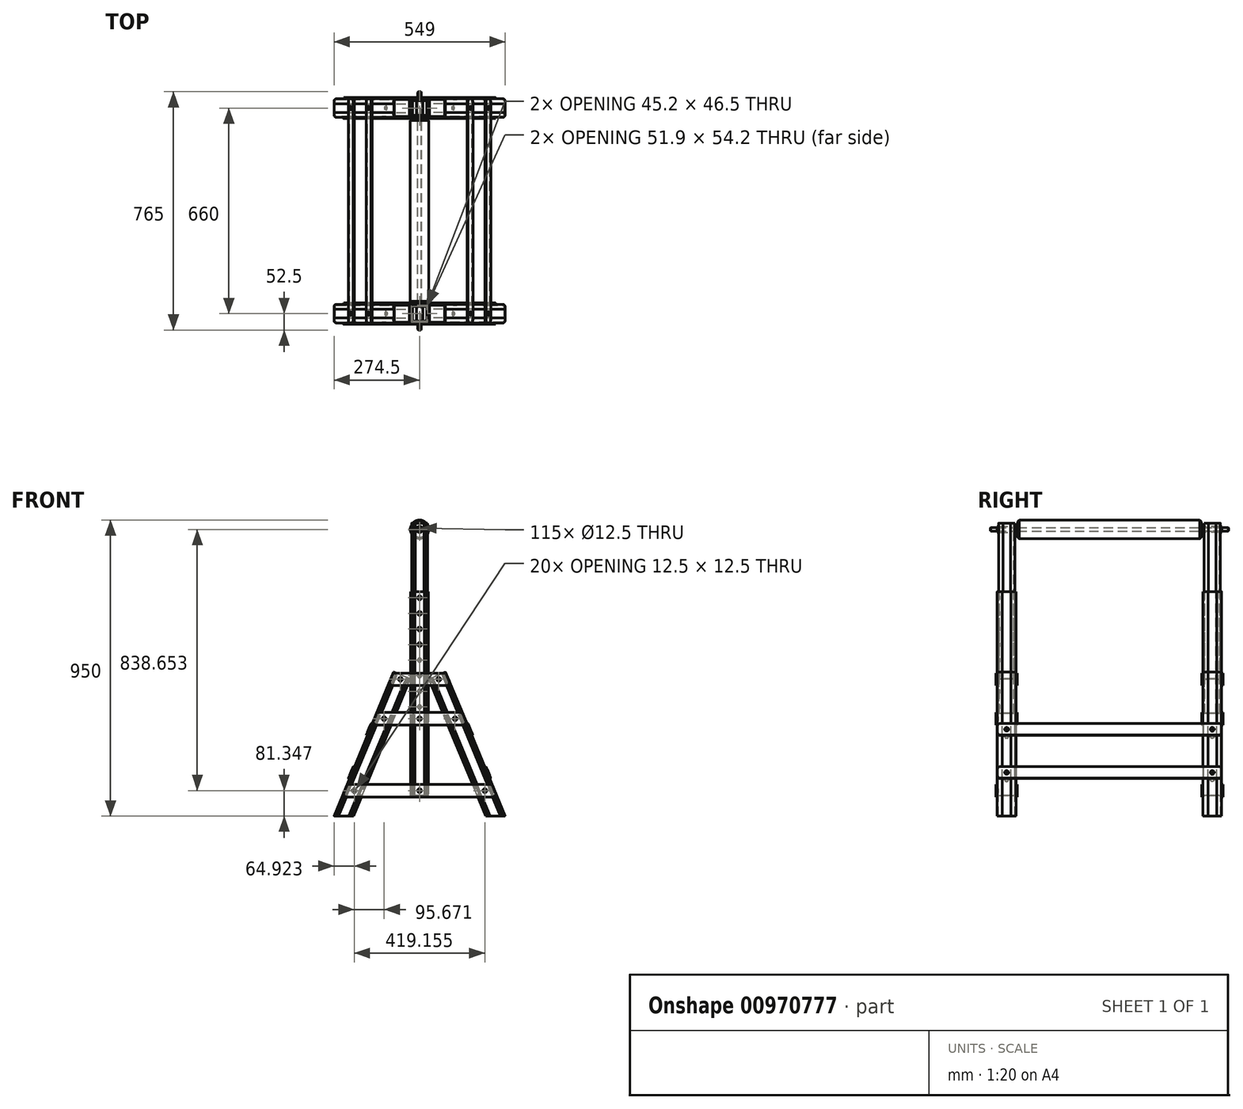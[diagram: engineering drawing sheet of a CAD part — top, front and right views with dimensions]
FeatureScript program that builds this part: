
annotation { "Feature Type Name" : "Feature", "Feature Type Description" : "" }
export const myFeature = defineFeature(function(context is Context, id is Id, definition is map)
    precondition{}
    {
        {
            var Q0;
            Q0=qCreatedBy(makeId("Front.planeOp"),FACE);
            var sketch = newSketch(context, id + "F0", { "sketchPlane" : qUnion([Q0])});
            skLineSegment(sketch, "E0", {"start": v(0, 0) * mm, "end": v(-62.45, 0) * mm});
            skLineSegment(sketch, "E1", {"start": v(-62.45, 0) * mm, "end": v(-244.65, 439.86) * mm});
            skLineSegment(sketch, "E2", {"start": v(-244.65, 439.86) * mm, "end": v(-191.34, 461.94) * mm});
            skLineSegment(sketch, "E3", {"start": v(-191.34, 461.94) * mm, "end": v(0, 0) * mm});
            skLineSegment(sketch, "E4", {"start": v(-218, 450.9) * mm, "end": v(-31.23, 0) * mm, "construction": true});
            skCircle(sketch, "E5", {"center": v(-213.02, 438.89) * mm, "radius": 6.25 * mm});
            skCircle(sketch, "E6", {"center": v(-64.92, 81.35) * mm, "radius": 6.25 * mm});
            skCircle(sketch, "E7", {"center": v(-160.6, 312.32) * mm, "radius": 6.25 * mm});
            skSolve(sketch);
        }
        {
            var Q0;
            Q0=qSketchRegion(id+"F0",true);
            extrude(context, id + "F1", {"entities" : qUnion([Q0]), "depth" : 60 * mm, "offsetDistance" : 25 * mm});
        }
        {
            var Q0;
            Q0=makeQuery(id+"F1.opExtrude","SWEPT_FACE",FACE,{"disambiguationData":[OSD([sQuery(id+"F0.wireOp",EDGE,"E3")])]});
            var sketch = newSketch(context, id + "F2", { "sketchPlane" : qUnion([Q0])});
            skLineSegment(sketch, "E8", {"start": v(-30, 500) * mm, "end": v(-30, 0) * mm, "construction": true});
            skCircle(sketch, "E9", {"center": v(-30, 150) * mm, "radius": 6.25 * mm});
            skCircle(sketch, "E10", {"center": v(-30, 300) * mm, "radius": 6.25 * mm});
            skSolve(sketch);
        }
        {
            var Q0;
            Q0=qSketchRegion(id+"F2",true);
            var Q1;
            Q1=makeQuery(id+"F1.opExtrude","SWEPT_FACE",FACE,{"disambiguationData":[OSD([sQuery(id+"F0.wireOp",EDGE,"E1")])]});
            extrude(context, id + "F3", {"entities" : qUnion([Q0]), "operationType" : NewBodyOperationType.REMOVE, "endBound" : BoundingType.UP_TO_SURFACE, "oppositeDirection" : true, "depth" : 25 * mm, "endBoundEntityFace" : qUnion([Q1]), "offsetDistance" : 25 * mm});
        }
        {
            var Q0;
            Q0=makeQuery(id+"F1.opExtrude","CAP_EDGE",EDGE,{"disambiguationData":[OSD([sQuery(id+"F0.wireOp",EDGE,"E1")])],"isStart":false});
            var Q1;
            Q1=makeQuery(id+"F1.opExtrude","CAP_EDGE",EDGE,{"disambiguationData":[OSD([sQuery(id+"F0.wireOp",EDGE,"E3")])],"isStart":false});
            var Q2;
            Q2=makeQuery(id+"F1.opExtrude","CAP_EDGE",EDGE,{"disambiguationData":[OSD([sQuery(id+"F0.wireOp",EDGE,"E1")])],"isStart":true});
            var Q3;
            Q3=makeQuery(id+"F1.opExtrude","CAP_EDGE",EDGE,{"disambiguationData":[OSD([sQuery(id+"F0.wireOp",EDGE,"E3")])],"isStart":true});
            fillet(context, id + "F4", {"entities" : qUnion([Q0, Q1, Q2, Q3]), "radius" : 7.5 * mm, "tangentPropagation" : true, "allowEdgeOverflow" : false});
        }
        {
            var Q0;
            Q0=makeQuery(id+"F1.opExtrude","SWEPT_FACE",FACE,{"disambiguationData":[OSD([sQuery(id+"F0.wireOp",EDGE,"E2")])]});
            var sketch = newSketch(context, id + "F5", { "sketchPlane" : qUnion([Q0])});
            skLineSegment(sketch, "E11", {"start": v(-57.7, -30) * mm, "end": v(-28.85, -30) * mm, "construction": true});
            skLineSegment(sketch, "E12", {"start": v(-28.85, -30) * mm, "end": v(-28.85, -60) * mm, "construction": true});
            skArc(sketch, "E13.0", {"start": v(-54.8, -52.5) * mm, "mid": v(-53.45, -55.75) * mm, "end": v(-50.2, -57.1) * mm});
            skLineSegment(sketch, "E14", {"start": v(-57.4, -30) * mm, "end": v(-57.4, -44) * mm});
            skLineSegment(sketch, "E15", {"start": v(-57.4, -44) * mm, "end": v(-57.7, -44) * mm});
            skLineSegment(sketch, "E16", {"start": v(-50.2, -60) * mm, "end": v(-49.2, -59) * mm});
            skLineSegment(sketch, "E17", {"start": v(-49.2, -59) * mm, "end": v(-48.2, -60) * mm});
            skLineSegment(sketch, "E18", {"start": v(-48.2, -60) * mm, "end": v(-47.2, -59) * mm});
            skLineSegment(sketch, "E19", {"start": v(-47.2, -59) * mm, "end": v(-46.2, -60) * mm});
            skLineSegment(sketch, "E20", {"start": v(-46.2, -60) * mm, "end": v(-45.2, -59) * mm});
            skLineSegment(sketch, "E21", {"start": v(-45.2, -59) * mm, "end": v(-44.2, -60) * mm});
            skLineSegment(sketch, "E22", {"start": v(-50.2, -57.1) * mm, "end": v(-28.85, -57.1) * mm});
            skLineSegment(sketch, "E23", {"start": v(-54.8, -52.5) * mm, "end": v(-54.8, -30) * mm});
            skLineSegment(sketch, "E24.MirrorCS", {"start": v(-0.3, -44) * mm, "end": v(0, -44) * mm});
            skLineSegment(sketch, "E25.MirrorCS", {"start": v(-12.5, -59) * mm, "end": v(-13.5, -60) * mm});
            skLineSegment(sketch, "E26.MirrorCS", {"start": v(-7.5, -60) * mm, "end": v(-8.5, -59) * mm});
            skLineSegment(sketch, "E27.MirrorCS", {"start": v(-8.5, -59) * mm, "end": v(-9.5, -60) * mm});
            skLineSegment(sketch, "E28.MirrorCS", {"start": v(-11.5, -60) * mm, "end": v(-12.5, -59) * mm});
            skLineSegment(sketch, "E29.MirrorCS", {"start": v(-10.5, -59) * mm, "end": v(-11.5, -60) * mm});
            skLineSegment(sketch, "E30.MirrorCS", {"start": v(-9.5, -60) * mm, "end": v(-10.5, -59) * mm});
            skLineSegment(sketch, "E31.MirrorCS", {"start": v(-0.3, -30) * mm, "end": v(-0.3, -44) * mm});
            skLineSegment(sketch, "E32.MirrorCS", {"start": v(-7.5, -57.1) * mm, "end": v(-28.85, -57.1) * mm});
            skLineSegment(sketch, "E33.MirrorCS", {"start": v(-2.9, -52.5) * mm, "end": v(-2.9, -30) * mm});
            skArc(sketch, "E34.MirrorCS", {"start": v(-2.9, -52.5) * mm, "mid": v(-4.25, -55.75) * mm, "end": v(-7.5, -57.1) * mm});
            skLineSegment(sketch, "E35.MirrorCS", {"start": v(-57.4, -16) * mm, "end": v(-57.7, -16) * mm});
            skLineSegment(sketch, "E36.MirrorCS", {"start": v(-50.2, 0) * mm, "end": v(-49.2, -1) * mm});
            skLineSegment(sketch, "E37.MirrorCS", {"start": v(-45.2, -1) * mm, "end": v(-44.2, 0) * mm});
            skLineSegment(sketch, "E38.MirrorCS", {"start": v(-47.2, -1) * mm, "end": v(-46.2, 0) * mm});
            skLineSegment(sketch, "E39.MirrorCS", {"start": v(-48.2, 0) * mm, "end": v(-47.2, -1) * mm});
            skLineSegment(sketch, "E40.MirrorCS", {"start": v(-49.2, -1) * mm, "end": v(-48.2, 0) * mm});
            skLineSegment(sketch, "E41.MirrorCS", {"start": v(-46.2, 0) * mm, "end": v(-45.2, -1) * mm});
            skLineSegment(sketch, "E42.MirrorCS", {"start": v(-57.4, -30) * mm, "end": v(-57.4, -16) * mm});
            skArc(sketch, "E43.MirrorCS", {"start": v(-54.8, -7.5) * mm, "mid": v(-53.45, -4.25) * mm, "end": v(-50.2, -2.9) * mm});
            skLineSegment(sketch, "E44.MirrorCS", {"start": v(-50.2, -2.9) * mm, "end": v(-28.85, -2.9) * mm});
            skLineSegment(sketch, "E45.MirrorCS", {"start": v(-54.8, -7.5) * mm, "end": v(-54.8, -30) * mm});
            skLineSegment(sketch, "E46.MirrorCS", {"start": v(-0.3, -16) * mm, "end": v(0, -16) * mm});
            skLineSegment(sketch, "E47.MirrorCS", {"start": v(-8.5, -1) * mm, "end": v(-9.5, 0) * mm});
            skLineSegment(sketch, "E48.MirrorCS", {"start": v(-11.5, 0) * mm, "end": v(-12.5, -1) * mm});
            skLineSegment(sketch, "E49.MirrorCS", {"start": v(-10.5, -1) * mm, "end": v(-11.5, 0) * mm});
            skLineSegment(sketch, "E50.MirrorCS", {"start": v(-9.5, 0) * mm, "end": v(-10.5, -1) * mm});
            skLineSegment(sketch, "E51.MirrorCS", {"start": v(-12.5, -1) * mm, "end": v(-13.5, 0) * mm});
            skLineSegment(sketch, "E52.MirrorCS", {"start": v(-7.5, 0) * mm, "end": v(-8.5, -1) * mm});
            skLineSegment(sketch, "E53.MirrorCS", {"start": v(-0.3, -30) * mm, "end": v(-0.3, -16) * mm});
            skLineSegment(sketch, "E54.MirrorCS", {"start": v(-2.9, -7.5) * mm, "end": v(-2.9, -30) * mm});
            skArc(sketch, "E55.MirrorCS", {"start": v(-2.9, -7.5) * mm, "mid": v(-4.25, -4.25) * mm, "end": v(-7.5, -2.9) * mm});
            skLineSegment(sketch, "E56.MirrorCS", {"start": v(-7.5, -2.9) * mm, "end": v(-28.85, -2.9) * mm});
            skSolve(sketch);
        }
        {
            var Q0;
            {var subQ0=sQuery(id+"F5.wireOp",EDGE,"E20");Q0=makeQuery(id+"F5.imprint","IMPRINT",FACE,{"disambiguationData":[TD([[makeQuery(id+"F5.imprint","IMPRINT",EDGE,{"derivedFrom":subQ0}),-1.0]])]});}
            var Q1;
            {var subQ0=sQuery(id+"F5.wireOp",EDGE,"E18");Q1=makeQuery(id+"F5.imprint","IMPRINT",FACE,{"disambiguationData":[TD([[makeQuery(id+"F5.imprint","IMPRINT",EDGE,{"derivedFrom":subQ0}),-1.0]])]});}
            var Q2;
            {var subQ0=sQuery(id+"F5.wireOp",EDGE,"E16");Q2=makeQuery(id+"F5.imprint","IMPRINT",FACE,{"disambiguationData":[TD([[makeQuery(id+"F5.imprint","IMPRINT",EDGE,{"derivedFrom":subQ0}),-1.0]])]});}
            var Q3;
            {var subQ0=sQuery(id+"F5.wireOp",EDGE,"E26.MirrorCS");Q3=makeQuery(id+"F5.imprint","IMPRINT",FACE,{"disambiguationData":[TD([[makeQuery(id+"F5.imprint","IMPRINT",EDGE,{"derivedFrom":subQ0}),1.0]])]});}
            var Q4;
            {var subQ0=sQuery(id+"F5.wireOp",EDGE,"E29.MirrorCS");Q4=makeQuery(id+"F5.imprint","IMPRINT",FACE,{"disambiguationData":[TD([[makeQuery(id+"F5.imprint","IMPRINT",EDGE,{"derivedFrom":subQ0}),1.0]])]});}
            var Q5;
            {var subQ0=sQuery(id+"F5.wireOp",EDGE,"E25.MirrorCS");Q5=makeQuery(id+"F5.imprint","IMPRINT",FACE,{"disambiguationData":[TD([[makeQuery(id+"F5.imprint","IMPRINT",EDGE,{"derivedFrom":subQ0}),1.0]])]});}
            var Q6;
            {var subQ1=sQuery(id+"F5.wireOp",EDGE,"E24.MirrorCS");Q6=makeQuery(id+"F5.imprint","IMPRINT",FACE,{"disambiguationData":[TD([[makeQuery(id+"F5.imprint","IMPRINT",EDGE,{"derivedFrom":subQ1}),1.0]])]});}
            var Q7;
            Q7=makeQuery(id+"F5.imprint","IMPRINT",FACE,{"disambiguationData":[TD([[makeQuery(id+"F5.imprint","IMPRINT",EDGE,{"derivedFrom":sQuery(id+"F5.wireOp",EDGE,"E14")}),-1.0]])]});
            var Q8;
            {var subQ0=sQuery(id+"F5.wireOp",EDGE,"E36.MirrorCS");Q8=makeQuery(id+"F5.imprint","IMPRINT",FACE,{"disambiguationData":[TD([[makeQuery(id+"F5.imprint","IMPRINT",EDGE,{"derivedFrom":subQ0}),1.0]])]});}
            var Q9;
            {var subQ0=sQuery(id+"F5.wireOp",EDGE,"E38.MirrorCS");Q9=makeQuery(id+"F5.imprint","IMPRINT",FACE,{"disambiguationData":[TD([[makeQuery(id+"F5.imprint","IMPRINT",EDGE,{"derivedFrom":subQ0}),1.0]])]});}
            var Q10;
            {var subQ0=sQuery(id+"F5.wireOp",EDGE,"E37.MirrorCS");Q10=makeQuery(id+"F5.imprint","IMPRINT",FACE,{"disambiguationData":[TD([[makeQuery(id+"F5.imprint","IMPRINT",EDGE,{"derivedFrom":subQ0}),1.0]])]});}
            var Q11;
            {var subQ0=sQuery(id+"F5.wireOp",EDGE,"E47.MirrorCS");Q11=makeQuery(id+"F5.imprint","IMPRINT",FACE,{"disambiguationData":[TD([[makeQuery(id+"F5.imprint","IMPRINT",EDGE,{"derivedFrom":subQ0}),-1.0]])]});}
            var Q12;
            {var subQ0=sQuery(id+"F5.wireOp",EDGE,"E49.MirrorCS");Q12=makeQuery(id+"F5.imprint","IMPRINT",FACE,{"disambiguationData":[TD([[makeQuery(id+"F5.imprint","IMPRINT",EDGE,{"derivedFrom":subQ0}),-1.0]])]});}
            var Q13;
            {var subQ0=sQuery(id+"F5.wireOp",EDGE,"E48.MirrorCS");Q13=makeQuery(id+"F5.imprint","IMPRINT",FACE,{"disambiguationData":[TD([[makeQuery(id+"F5.imprint","IMPRINT",EDGE,{"derivedFrom":subQ0}),-1.0]])]});}
            var Q14;
            Q14=makeQuery(id+"F5.imprint","IMPRINT",FACE,{"disambiguationData":[TD([[makeQuery(id+"F5.imprint","IMPRINT",EDGE,{"derivedFrom":sQuery(id+"F5.wireOp",EDGE,"E13.0")}),1.0]])]});
            var Q15;
            Q15=makeQuery(id+"F1.opExtrude","SWEPT_FACE",FACE,{"disambiguationData":[OSD([sQuery(id+"F0.wireOp",EDGE,"E0")])]});
            extrude(context, id + "F6", {"entities" : qUnion([Q0, Q1, Q2, Q3, Q4, Q5, Q6, Q7, Q8, Q9, Q10, Q11, Q12, Q13, Q14]), "operationType" : NewBodyOperationType.REMOVE, "endBound" : BoundingType.UP_TO_SURFACE, "oppositeDirection" : true, "depth" : 25 * mm, "endBoundEntityFace" : qUnion([Q15]), "offsetDistance" : 25 * mm});
        }
        {
            var Q0;
            Q0=makeQuery(id+"F1.opExtrude","CAP_FACE",FACE,{"disambiguationData":[OSD([sQuery(id+"F0.wireOp",EDGE,"E0"),sQuery(id+"F0.wireOp",EDGE,"E1"),sQuery(id+"F0.wireOp",EDGE,"E2"),sQuery(id+"F0.wireOp",EDGE,"E3"),sQuery(id+"F0.wireOp",EDGE,"E5"),sQuery(id+"F0.wireOp",EDGE,"E6")])],"isStart":false});
            var sketch = newSketch(context, id + "F7", { "sketchPlane" : qUnion([Q0])});
            skLineSegment(sketch, "E57", {"start": v(-245.65, 720.32) * mm, "end": v(-245.65, 66.32) * mm});
            skLineSegment(sketch, "E58", {"start": v(-245.65, 66.32) * mm, "end": v(-303.35, 66.32) * mm});
            skLineSegment(sketch, "E59", {"start": v(-303.35, 66.32) * mm, "end": v(-303.35, 720.32) * mm});
            skLineSegment(sketch, "E60", {"start": v(-303.35, 720.32) * mm, "end": v(-245.65, 720.32) * mm});
            skLineSegment(sketch, "E61", {"start": v(-303.35, 75.1) * mm, "end": v(24.53, 75.1) * mm, "construction": true});
            skLineSegment(sketch, "E62", {"start": v(-274.5, 720.32) * mm, "end": v(-274.5, 66.32) * mm, "construction": true});
            skCircle(sketch, "E63", {"center": v(-274.5, 81.35) * mm, "radius": 6.25 * mm});
            skLineSegment(sketch, "E64", {"start": v(-303.35, 306.07) * mm, "end": v(155.56, 306.07) * mm, "construction": true});
            skCircle(sketch, "E65", {"center": v(-274.5, 312.32) * mm, "radius": 6.25 * mm});
            skCircle(sketch, "E66", {"center": v(-274.5, 650.32) * mm, "radius": 6.25 * mm});
            skCircle(sketch, "E67", {"center": v(-274.5, 600.32) * mm, "radius": 6.25 * mm});
            skCircle(sketch, "E68", {"center": v(-274.5, 700.32) * mm, "radius": 6.25 * mm});
            skCircle(sketch, "E69", {"center": v(-274.5, 550.32) * mm, "radius": 6.25 * mm});
            skSolve(sketch);
        }
        {
            var Q0;
            Q0=qSketchRegion(id+"F7",true);
            extrude(context, id + "F8", {"entities" : qUnion([Q0]), "oppositeDirection" : true, "depth" : 60 * mm, "offsetDistance" : 25 * mm});
        }
        {
            var Q0;
            Q0=makeQuery(id+"F8.opExtrude","CAP_EDGE",EDGE,{"disambiguationData":[OSD([sQuery(id+"F7.wireOp",EDGE,"E59")])],"isStart":false});
            var Q1;
            Q1=makeQuery(id+"F8.opExtrude","CAP_EDGE",EDGE,{"disambiguationData":[OSD([sQuery(id+"F7.wireOp",EDGE,"E59")])],"isStart":true});
            var Q2;
            Q2=makeQuery(id+"F8.opExtrude","CAP_EDGE",EDGE,{"disambiguationData":[OSD([sQuery(id+"F7.wireOp",EDGE,"E57")])],"isStart":true});
            var Q3;
            Q3=makeQuery(id+"F8.opExtrude","CAP_EDGE",EDGE,{"disambiguationData":[OSD([sQuery(id+"F7.wireOp",EDGE,"E57")])],"isStart":false});
            fillet(context, id + "F9", {"entities" : qUnion([Q0, Q1, Q2, Q3]), "radius" : 7.5 * mm, "tangentPropagation" : true, "allowEdgeOverflow" : false});
        }
        {
            var Q0;
            Q0=makeQuery(id+"F8.opExtrude","SWEPT_FACE",FACE,{"disambiguationData":[OSD([sQuery(id+"F7.wireOp",EDGE,"E60")])]});
            var sketch = newSketch(context, id + "F10", { "sketchPlane" : qUnion([Q0])});
            skLineSegment(sketch, "E70", {"start": v(-274.5, -60) * mm, "end": v(-274.5, -30) * mm, "construction": true});
            skPoint(sketch, "E70.endSnap0", {"position": v(-303.35, -30) * mm});
            skLineSegment(sketch, "E71", {"start": v(-274.5, -30) * mm, "end": v(-303.35, -30) * mm, "construction": true});
            skLineSegment(sketch, "E72", {"start": v(-295.85, -60) * mm, "end": v(-294.85, -59) * mm});
            skLineSegment(sketch, "E73", {"start": v(-294.85, -59) * mm, "end": v(-293.85, -60) * mm});
            skLineSegment(sketch, "E74", {"start": v(-293.85, -60) * mm, "end": v(-292.85, -59) * mm});
            skLineSegment(sketch, "E75", {"start": v(-292.85, -59) * mm, "end": v(-291.85, -60) * mm});
            skLineSegment(sketch, "E76", {"start": v(-291.85, -60) * mm, "end": v(-290.85, -59) * mm});
            skLineSegment(sketch, "E77", {"start": v(-290.85, -59) * mm, "end": v(-289.85, -60) * mm});
            skLineSegment(sketch, "E78", {"start": v(-303.05, -30) * mm, "end": v(-303.05, -44) * mm});
            skLineSegment(sketch, "E79", {"start": v(-303.05, -44) * mm, "end": v(-303.35, -44) * mm});
            skArc(sketch, "E80.0", {"start": v(-300.45, -52.5) * mm, "mid": v(-299.1, -55.75) * mm, "end": v(-295.85, -57.1) * mm});
            skLineSegment(sketch, "E81", {"start": v(-295.85, -57.1) * mm, "end": v(-274.5, -57.1) * mm});
            skLineSegment(sketch, "E82", {"start": v(-300.45, -52.5) * mm, "end": v(-300.45, -30) * mm});
            skLineSegment(sketch, "E83.MirrorCS", {"start": v(-255.15, -60) * mm, "end": v(-256.15, -59) * mm});
            skLineSegment(sketch, "E84.MirrorCS", {"start": v(-245.95, -44) * mm, "end": v(-245.65, -44) * mm});
            skLineSegment(sketch, "E85.MirrorCS", {"start": v(-254.15, -59) * mm, "end": v(-255.15, -60) * mm});
            skLineSegment(sketch, "E86.MirrorCS", {"start": v(-256.15, -59) * mm, "end": v(-257.15, -60) * mm});
            skLineSegment(sketch, "E87.MirrorCS", {"start": v(-257.15, -60) * mm, "end": v(-258.15, -59) * mm});
            skLineSegment(sketch, "E88.MirrorCS", {"start": v(-253.15, -60) * mm, "end": v(-254.15, -59) * mm});
            skLineSegment(sketch, "E89.MirrorCS", {"start": v(-258.15, -59) * mm, "end": v(-259.15, -60) * mm});
            skLineSegment(sketch, "E90.MirrorCS", {"start": v(-248.55, -52.5) * mm, "end": v(-248.55, -30) * mm});
            skLineSegment(sketch, "E91.MirrorCS", {"start": v(-245.95, -30) * mm, "end": v(-245.95, -44) * mm});
            skLineSegment(sketch, "E92.MirrorCS", {"start": v(-253.15, -57.1) * mm, "end": v(-274.5, -57.1) * mm});
            skArc(sketch, "E93.MirrorCS", {"start": v(-248.55, -52.5) * mm, "mid": v(-249.9, -55.75) * mm, "end": v(-253.15, -57.1) * mm});
            skLineSegment(sketch, "E94.MirrorCS", {"start": v(-290.85, -1) * mm, "end": v(-289.85, 0) * mm});
            skLineSegment(sketch, "E95.MirrorCS", {"start": v(-303.05, -16) * mm, "end": v(-303.35, -16) * mm});
            skLineSegment(sketch, "E96.MirrorCS", {"start": v(-295.85, 0) * mm, "end": v(-294.85, -1) * mm});
            skLineSegment(sketch, "E97.MirrorCS", {"start": v(-293.85, 0) * mm, "end": v(-292.85, -1) * mm});
            skLineSegment(sketch, "E98.MirrorCS", {"start": v(-294.85, -1) * mm, "end": v(-293.85, 0) * mm});
            skLineSegment(sketch, "E99.MirrorCS", {"start": v(-291.85, 0) * mm, "end": v(-290.85, -1) * mm});
            skLineSegment(sketch, "E100.MirrorCS", {"start": v(-292.85, -1) * mm, "end": v(-291.85, 0) * mm});
            skLineSegment(sketch, "E101.MirrorCS", {"start": v(-300.45, -7.5) * mm, "end": v(-300.45, -30) * mm});
            skLineSegment(sketch, "E102.MirrorCS", {"start": v(-295.85, -2.9) * mm, "end": v(-274.5, -2.9) * mm});
            skArc(sketch, "E103.MirrorCS", {"start": v(-300.45, -7.5) * mm, "mid": v(-299.1, -4.25) * mm, "end": v(-295.85, -2.9) * mm});
            skLineSegment(sketch, "E104.MirrorCS", {"start": v(-303.05, -30) * mm, "end": v(-303.05, -16) * mm});
            skLineSegment(sketch, "E105.MirrorCS", {"start": v(-253.15, 0) * mm, "end": v(-254.15, -1) * mm});
            skLineSegment(sketch, "E106.MirrorCS", {"start": v(-258.15, -1) * mm, "end": v(-259.15, 0) * mm});
            skLineSegment(sketch, "E107.MirrorCS", {"start": v(-255.15, 0) * mm, "end": v(-256.15, -1) * mm});
            skLineSegment(sketch, "E108.MirrorCS", {"start": v(-257.15, 0) * mm, "end": v(-258.15, -1) * mm});
            skLineSegment(sketch, "E109.MirrorCS", {"start": v(-256.15, -1) * mm, "end": v(-257.15, 0) * mm});
            skLineSegment(sketch, "E110.MirrorCS", {"start": v(-245.95, -16) * mm, "end": v(-245.65, -16) * mm});
            skLineSegment(sketch, "E111.MirrorCS", {"start": v(-254.15, -1) * mm, "end": v(-255.15, 0) * mm});
            skLineSegment(sketch, "E112.MirrorCS", {"start": v(-248.55, -7.5) * mm, "end": v(-248.55, -30) * mm});
            skLineSegment(sketch, "E113.MirrorCS", {"start": v(-245.95, -30) * mm, "end": v(-245.95, -16) * mm});
            skArc(sketch, "E114.MirrorCS", {"start": v(-248.55, -7.5) * mm, "mid": v(-249.9, -4.25) * mm, "end": v(-253.15, -2.9) * mm});
            skLineSegment(sketch, "E115.MirrorCS", {"start": v(-253.15, -2.9) * mm, "end": v(-274.5, -2.9) * mm});
            skSolve(sketch);
        }
        {
            var Q0;
            {var subQ0=sQuery(id+"F10.wireOp",EDGE,"E76");Q0=makeQuery(id+"F10.imprint","IMPRINT",FACE,{"disambiguationData":[TD([[makeQuery(id+"F10.imprint","IMPRINT",EDGE,{"derivedFrom":subQ0}),-1.0]])]});}
            var Q1;
            {var subQ0=sQuery(id+"F10.wireOp",EDGE,"E74");Q1=makeQuery(id+"F10.imprint","IMPRINT",FACE,{"disambiguationData":[TD([[makeQuery(id+"F10.imprint","IMPRINT",EDGE,{"derivedFrom":subQ0}),-1.0]])]});}
            var Q2;
            {var subQ0=sQuery(id+"F10.wireOp",EDGE,"E72");Q2=makeQuery(id+"F10.imprint","IMPRINT",FACE,{"disambiguationData":[TD([[makeQuery(id+"F10.imprint","IMPRINT",EDGE,{"derivedFrom":subQ0}),-1.0]])]});}
            var Q3;
            Q3=makeQuery(id+"F10.imprint","IMPRINT",FACE,{"disambiguationData":[TD([[makeQuery(id+"F10.imprint","IMPRINT",EDGE,{"derivedFrom":sQuery(id+"F10.wireOp",EDGE,"E78")}),-1.0]])]});
            var Q4;
            {var subQ0=sQuery(id+"F10.wireOp",EDGE,"E85.MirrorCS");Q4=makeQuery(id+"F10.imprint","IMPRINT",FACE,{"disambiguationData":[TD([[makeQuery(id+"F10.imprint","IMPRINT",EDGE,{"derivedFrom":subQ0}),1.0]])]});}
            var Q5;
            {var subQ0=sQuery(id+"F10.wireOp",EDGE,"E83.MirrorCS");Q5=makeQuery(id+"F10.imprint","IMPRINT",FACE,{"disambiguationData":[TD([[makeQuery(id+"F10.imprint","IMPRINT",EDGE,{"derivedFrom":subQ0}),1.0]])]});}
            var Q6;
            {var subQ0=sQuery(id+"F10.wireOp",EDGE,"E87.MirrorCS");Q6=makeQuery(id+"F10.imprint","IMPRINT",FACE,{"disambiguationData":[TD([[makeQuery(id+"F10.imprint","IMPRINT",EDGE,{"derivedFrom":subQ0}),1.0]])]});}
            var Q7;
            {var subQ1=sQuery(id+"F10.wireOp",EDGE,"E84.MirrorCS");Q7=makeQuery(id+"F10.imprint","IMPRINT",FACE,{"disambiguationData":[TD([[makeQuery(id+"F10.imprint","IMPRINT",EDGE,{"derivedFrom":subQ1}),1.0]])]});}
            var Q8;
            {var subQ0=sQuery(id+"F10.wireOp",EDGE,"E105.MirrorCS");Q8=makeQuery(id+"F10.imprint","IMPRINT",FACE,{"disambiguationData":[TD([[makeQuery(id+"F10.imprint","IMPRINT",EDGE,{"derivedFrom":subQ0}),-1.0]])]});}
            var Q9;
            {var subQ0=sQuery(id+"F10.wireOp",EDGE,"E107.MirrorCS");Q9=makeQuery(id+"F10.imprint","IMPRINT",FACE,{"disambiguationData":[TD([[makeQuery(id+"F10.imprint","IMPRINT",EDGE,{"derivedFrom":subQ0}),-1.0]])]});}
            var Q10;
            {var subQ0=sQuery(id+"F10.wireOp",EDGE,"E106.MirrorCS");Q10=makeQuery(id+"F10.imprint","IMPRINT",FACE,{"disambiguationData":[TD([[makeQuery(id+"F10.imprint","IMPRINT",EDGE,{"derivedFrom":subQ0}),-1.0]])]});}
            var Q11;
            {var subQ0=sQuery(id+"F10.wireOp",EDGE,"E96.MirrorCS");Q11=makeQuery(id+"F10.imprint","IMPRINT",FACE,{"disambiguationData":[TD([[makeQuery(id+"F10.imprint","IMPRINT",EDGE,{"derivedFrom":subQ0}),1.0]])]});}
            var Q12;
            {var subQ0=sQuery(id+"F10.wireOp",EDGE,"E97.MirrorCS");Q12=makeQuery(id+"F10.imprint","IMPRINT",FACE,{"disambiguationData":[TD([[makeQuery(id+"F10.imprint","IMPRINT",EDGE,{"derivedFrom":subQ0}),1.0]])]});}
            var Q13;
            {var subQ0=sQuery(id+"F10.wireOp",EDGE,"E94.MirrorCS");Q13=makeQuery(id+"F10.imprint","IMPRINT",FACE,{"disambiguationData":[TD([[makeQuery(id+"F10.imprint","IMPRINT",EDGE,{"derivedFrom":subQ0}),1.0]])]});}
            var Q14;
            Q14=makeQuery(id+"F10.imprint","IMPRINT",FACE,{"disambiguationData":[TD([[makeQuery(id+"F10.imprint","IMPRINT",EDGE,{"derivedFrom":sQuery(id+"F10.wireOp",EDGE,"E80.0")}),1.0]])]});
            var Q15;
            Q15=makeQuery(id+"F8.opExtrude","SWEPT_FACE",FACE,{"disambiguationData":[OSD([sQuery(id+"F7.wireOp",EDGE,"E58")])]});
            extrude(context, id + "F11", {"entities" : qUnion([Q0, Q1, Q2, Q3, Q4, Q5, Q6, Q7, Q8, Q9, Q10, Q11, Q12, Q13, Q14]), "operationType" : NewBodyOperationType.REMOVE, "endBound" : BoundingType.UP_TO_SURFACE, "oppositeDirection" : true, "depth" : 25 * mm, "endBoundEntityFace" : qUnion([Q15]), "offsetDistance" : 25 * mm});
        }
        {
            var Q0;
            {var subQ0=sQuery(id+"F7.wireOp",EDGE,"E59");Q0=makeQuery(id+"F11.boolean.opBoolean","SPLIT",FACE,{"disambiguationData":[TD([makeQuery(id+"F11.opExtrude","SWEPT_FACE",FACE,{"disambiguationData":[OSD([sQuery(id+"F10.wireOp",EDGE,"E95.MirrorCS")])]})])],"derivedFrom":makeQuery(id+"F8.opExtrude","SWEPT_FACE",FACE,{"disambiguationData":[OSD([subQ0])]})});}
            var Q1;
            {var subQ0=sQuery(id+"F7.wireOp",EDGE,"E57");Q1=makeQuery(id+"F11.boolean.opBoolean","SPLIT",FACE,{"disambiguationData":[TD([makeQuery(id+"F11.opExtrude","SWEPT_FACE",FACE,{"disambiguationData":[OSD([sQuery(id+"F10.wireOp",EDGE,"E110.MirrorCS")])]})])],"derivedFrom":makeQuery(id+"F8.opExtrude","SWEPT_FACE",FACE,{"disambiguationData":[OSD([subQ0])]})});}
            cPlane(context, id + "F12", {"entities" : qUnion([Q0, Q1]), "cplaneType" : CPlaneType.MID_PLANE, "offset" : 25 * mm, "width" : 150 * mm, "height" : 150 * mm});
        }
        {
            var Q0;
            Q0=makeQuery(id+"F11.boolean.opBoolean","COPY",FACE,{"derivedFrom":makeQuery(id+"F11.opExtrude","SWEPT_FACE",FACE,{"disambiguationData":[OSD([sQuery(id+"F10.wireOp",EDGE,"E81"),sQuery(id+"F10.wireOp",EDGE,"E92.MirrorCS")])]})});
            var Q1;
            Q1=makeQuery(id+"F11.boolean.opBoolean","COPY",FACE,{"derivedFrom":makeQuery(id+"F11.opExtrude","SWEPT_FACE",FACE,{"disambiguationData":[OSD([sQuery(id+"F10.wireOp",EDGE,"E102.MirrorCS"),sQuery(id+"F10.wireOp",EDGE,"E115.MirrorCS")])]})});
            cPlane(context, id + "F13", {"entities" : qUnion([Q0, Q1]), "cplaneType" : CPlaneType.MID_PLANE, "offset" : 25 * mm, "width" : 150 * mm, "height" : 150 * mm});
        }
        {
            var Q0;
            Q0=makeQuery(id+"F8.opExtrude","CAP_EDGE",EDGE,{"disambiguationData":[OSD([sQuery(id+"F7.wireOp",EDGE,"E65")])],"isStart":false});
            cPlane(context, id + "F14", {"entities" : qUnion([Q0]), "cplaneType" : CPlaneType.LINE_ANGLE, "offset" : 25 * mm, "angle" : 0 * degree, "width" : 150 * mm, "height" : 150 * mm});
        }
        {
            var Q0;
            Q0=qCreatedBy(id+"F13.planeOp",FACE);
            var sketch = newSketch(context, id + "F15", { "sketchPlane" : qUnion([Q0])});
            skLineSegment(sketch, "E116", {"start": v(249, 940.32) * mm, "end": v(249, 330.32) * mm});
            skLineSegment(sketch, "E117", {"start": v(249, 330.32) * mm, "end": v(300, 330.32) * mm});
            skLineSegment(sketch, "E118", {"start": v(300, 330.32) * mm, "end": v(300, 940.32) * mm});
            skLineSegment(sketch, "E119", {"start": v(300, 940.32) * mm, "end": v(249, 940.32) * mm});
            skLineSegment(sketch, "E120", {"start": v(274.5, 940.32) * mm, "end": v(274.5, 330.32) * mm, "construction": true});
            skCircle(sketch, "E121", {"center": v(274.5, 550.32) * mm, "radius": 6.25 * mm});
            skCircle(sketch, "E122", {"center": v(274.5, 500.32) * mm, "radius": 6.25 * mm});
            skCircle(sketch, "E123", {"center": v(274.5, 650.32) * mm, "radius": 6.25 * mm});
            skCircle(sketch, "E124", {"center": v(274.5, 450.32) * mm, "radius": 6.25 * mm});
            skCircle(sketch, "E125", {"center": v(274.5, 700.32) * mm, "radius": 6.25 * mm});
            skCircle(sketch, "E126", {"center": v(274.5, 600.32) * mm, "radius": 6.25 * mm});
            skCircle(sketch, "E127", {"center": v(274.5, 400.32) * mm, "radius": 6.25 * mm});
            skCircle(sketch, "E128", {"center": v(274.5, 350.32) * mm, "radius": 6.25 * mm});
            skCircle(sketch, "E129", {"center": v(274.5, 920) * mm, "radius": 10 * mm});
            skSolve(sketch);
        }
        {
            var Q0;
            Q0=qSketchRegion(id+"F15",true);
            extrude(context, id + "F16", {"entities" : qUnion([Q0]), "depth" : 52.3 * mm, "offsetDistance" : 25 * mm, "symmetric" : true});
        }
        {
            var Q0;
            Q0=makeQuery(id+"F16.opExtrude","CAP_EDGE",EDGE,{"disambiguationData":[OSD([sQuery(id+"F15.wireOp",EDGE,"E116")])],"isStart":true});
            var Q1;
            Q1=makeQuery(id+"F16.opExtrude","CAP_EDGE",EDGE,{"disambiguationData":[OSD([sQuery(id+"F15.wireOp",EDGE,"E118")])],"isStart":true});
            var Q2;
            Q2=makeQuery(id+"F16.opExtrude","CAP_EDGE",EDGE,{"disambiguationData":[OSD([sQuery(id+"F15.wireOp",EDGE,"E116")])],"isStart":false});
            var Q3;
            Q3=makeQuery(id+"F16.opExtrude","CAP_EDGE",EDGE,{"disambiguationData":[OSD([sQuery(id+"F15.wireOp",EDGE,"E118")])],"isStart":false});
            fillet(context, id + "F17", {"entities" : qUnion([Q0, Q1, Q2, Q3]), "radius" : 7.5 * mm, "tangentPropagation" : true, "allowEdgeOverflow" : false});
        }
        {
            var Q0;
            Q0=makeQuery(id+"F16.opExtrude","SWEPT_FACE",FACE,{"disambiguationData":[OSD([sQuery(id+"F15.wireOp",EDGE,"E119")])]});
            var sketch = newSketch(context, id + "F18", { "sketchPlane" : qUnion([Q0])});
            skLineSegment(sketch, "E130", {"start": v(-249, -30) * mm, "end": v(-274.5, -30) * mm, "construction": true});
            skPoint(sketch, "E130.endSnap0", {"position": v(-274.5, -3.85) * mm});
            skLineSegment(sketch, "E131", {"start": v(-274.5, -30) * mm, "end": v(-274.5, -3.85) * mm, "construction": true});
            skLineSegment(sketch, "E132", {"start": v(-256.5, -3.85) * mm, "end": v(-257.5, -4.85) * mm});
            skLineSegment(sketch, "E133", {"start": v(-257.5, -4.85) * mm, "end": v(-258.5, -3.85) * mm});
            skLineSegment(sketch, "E134", {"start": v(-258.5, -3.85) * mm, "end": v(-259.5, -4.85) * mm});
            skLineSegment(sketch, "E135", {"start": v(-259.5, -4.85) * mm, "end": v(-260.5, -3.85) * mm});
            skLineSegment(sketch, "E136", {"start": v(-249.25, -30) * mm, "end": v(-249.25, -17.85) * mm});
            skLineSegment(sketch, "E137", {"start": v(-249.25, -17.85) * mm, "end": v(-249, -17.85) * mm});
            skArc(sketch, "E138.0", {"start": v(-251.9, -11.35) * mm, "mid": v(-253.25, -8.1) * mm, "end": v(-256.5, -6.75) * mm});
            skLineSegment(sketch, "E139", {"start": v(-256.5, -6.75) * mm, "end": v(-274.5, -6.75) * mm});
            skLineSegment(sketch, "E140", {"start": v(-251.9, -11.35) * mm, "end": v(-251.9, -30) * mm});
            skLineSegment(sketch, "E141.MirrorCS", {"start": v(-299.75, -17.85) * mm, "end": v(-300, -17.85) * mm});
            skLineSegment(sketch, "E142.MirrorCS", {"start": v(-292.5, -3.85) * mm, "end": v(-291.5, -4.85) * mm});
            skLineSegment(sketch, "E143.MirrorCS", {"start": v(-290.5, -3.85) * mm, "end": v(-289.5, -4.85) * mm});
            skLineSegment(sketch, "E144.MirrorCS", {"start": v(-289.5, -4.85) * mm, "end": v(-288.5, -3.85) * mm});
            skLineSegment(sketch, "E145.MirrorCS", {"start": v(-291.5, -4.85) * mm, "end": v(-290.5, -3.85) * mm});
            skLineSegment(sketch, "E146.MirrorCS", {"start": v(-299.75, -30) * mm, "end": v(-299.75, -17.85) * mm});
            skLineSegment(sketch, "E147.MirrorCS", {"start": v(-297.1, -11.35) * mm, "end": v(-297.1, -30) * mm});
            skLineSegment(sketch, "E148.MirrorCS", {"start": v(-292.5, -6.75) * mm, "end": v(-274.5, -6.75) * mm});
            skArc(sketch, "E149.MirrorCS", {"start": v(-297.1, -11.35) * mm, "mid": v(-295.75, -8.1) * mm, "end": v(-292.5, -6.75) * mm});
            skLineSegment(sketch, "E150.MirrorCS", {"start": v(-258.5, -56.15) * mm, "end": v(-259.5, -55.15) * mm});
            skLineSegment(sketch, "E151.MirrorCS", {"start": v(-249.25, -42.15) * mm, "end": v(-249, -42.15) * mm});
            skLineSegment(sketch, "E152.MirrorCS", {"start": v(-257.5, -55.15) * mm, "end": v(-258.5, -56.15) * mm});
            skLineSegment(sketch, "E153.MirrorCS", {"start": v(-256.5, -56.15) * mm, "end": v(-257.5, -55.15) * mm});
            skLineSegment(sketch, "E154.MirrorCS", {"start": v(-259.5, -55.15) * mm, "end": v(-260.5, -56.15) * mm});
            skLineSegment(sketch, "E155.MirrorCS", {"start": v(-256.5, -53.25) * mm, "end": v(-274.5, -53.25) * mm});
            skArc(sketch, "E156.MirrorCS", {"start": v(-251.9, -48.65) * mm, "mid": v(-253.25, -51.9) * mm, "end": v(-256.5, -53.25) * mm});
            skLineSegment(sketch, "E157.MirrorCS", {"start": v(-249.25, -30) * mm, "end": v(-249.25, -42.15) * mm});
            skLineSegment(sketch, "E158.MirrorCS", {"start": v(-251.9, -48.65) * mm, "end": v(-251.9, -30) * mm});
            skLineSegment(sketch, "E159.MirrorCS", {"start": v(-299.75, -42.15) * mm, "end": v(-300, -42.15) * mm});
            skLineSegment(sketch, "E160.MirrorCS", {"start": v(-291.5, -55.15) * mm, "end": v(-290.5, -56.15) * mm});
            skLineSegment(sketch, "E161.MirrorCS", {"start": v(-290.5, -56.15) * mm, "end": v(-289.5, -55.15) * mm});
            skLineSegment(sketch, "E162.MirrorCS", {"start": v(-292.5, -56.15) * mm, "end": v(-291.5, -55.15) * mm});
            skLineSegment(sketch, "E163.MirrorCS", {"start": v(-289.5, -55.15) * mm, "end": v(-288.5, -56.15) * mm});
            skLineSegment(sketch, "E164.MirrorCS", {"start": v(-299.75, -30) * mm, "end": v(-299.75, -42.15) * mm});
            skArc(sketch, "E165.MirrorCS", {"start": v(-297.1, -48.65) * mm, "mid": v(-295.75, -51.9) * mm, "end": v(-292.5, -53.25) * mm});
            skLineSegment(sketch, "E166.MirrorCS", {"start": v(-297.1, -48.65) * mm, "end": v(-297.1, -30) * mm});
            skLineSegment(sketch, "E167.MirrorCS", {"start": v(-292.5, -53.25) * mm, "end": v(-274.5, -53.25) * mm});
            skSolve(sketch);
        }
        {
            var Q0;
            Q0=makeQuery(id+"F18.imprint","IMPRINT",FACE,{"disambiguationData":[TD([[makeQuery(id+"F18.imprint","IMPRINT",EDGE,{"derivedFrom":sQuery(id+"F18.wireOp",EDGE,"E136")}),-1.0]])]});
            var Q1;
            {var subQ1=sQuery(id+"F18.wireOp",EDGE,"E141.MirrorCS");Q1=makeQuery(id+"F18.imprint","IMPRINT",FACE,{"disambiguationData":[TD([[makeQuery(id+"F18.imprint","IMPRINT",EDGE,{"derivedFrom":subQ1}),1.0]])]});}
            var Q2;
            {var subQ0=sQuery(id+"F18.wireOp",EDGE,"E160.MirrorCS");Q2=makeQuery(id+"F18.imprint","IMPRINT",FACE,{"disambiguationData":[TD([[makeQuery(id+"F18.imprint","IMPRINT",EDGE,{"derivedFrom":subQ0}),-1.0]])]});}
            var Q3;
            {var subQ0=sQuery(id+"F18.wireOp",EDGE,"E161.MirrorCS");Q3=makeQuery(id+"F18.imprint","IMPRINT",FACE,{"disambiguationData":[TD([[makeQuery(id+"F18.imprint","IMPRINT",EDGE,{"derivedFrom":subQ0}),-1.0]])]});}
            var Q4;
            {var subQ0=sQuery(id+"F18.wireOp",EDGE,"E152.MirrorCS");Q4=makeQuery(id+"F18.imprint","IMPRINT",FACE,{"disambiguationData":[TD([[makeQuery(id+"F18.imprint","IMPRINT",EDGE,{"derivedFrom":subQ0}),1.0]])]});}
            var Q5;
            {var subQ0=sQuery(id+"F18.wireOp",EDGE,"E150.MirrorCS");Q5=makeQuery(id+"F18.imprint","IMPRINT",FACE,{"disambiguationData":[TD([[makeQuery(id+"F18.imprint","IMPRINT",EDGE,{"derivedFrom":subQ0}),1.0]])]});}
            var Q6;
            {var subQ0=sQuery(id+"F18.wireOp",EDGE,"E132");Q6=makeQuery(id+"F18.imprint","IMPRINT",FACE,{"disambiguationData":[TD([[makeQuery(id+"F18.imprint","IMPRINT",EDGE,{"derivedFrom":subQ0}),-1.0]])]});}
            var Q7;
            {var subQ0=sQuery(id+"F18.wireOp",EDGE,"E134");Q7=makeQuery(id+"F18.imprint","IMPRINT",FACE,{"disambiguationData":[TD([[makeQuery(id+"F18.imprint","IMPRINT",EDGE,{"derivedFrom":subQ0}),-1.0]])]});}
            var Q8;
            {var subQ0=sQuery(id+"F18.wireOp",EDGE,"E142.MirrorCS");Q8=makeQuery(id+"F18.imprint","IMPRINT",FACE,{"disambiguationData":[TD([[makeQuery(id+"F18.imprint","IMPRINT",EDGE,{"derivedFrom":subQ0}),1.0]])]});}
            var Q9;
            {var subQ0=sQuery(id+"F18.wireOp",EDGE,"E143.MirrorCS");Q9=makeQuery(id+"F18.imprint","IMPRINT",FACE,{"disambiguationData":[TD([[makeQuery(id+"F18.imprint","IMPRINT",EDGE,{"derivedFrom":subQ0}),1.0]])]});}
            var Q10;
            Q10=makeQuery(id+"F18.imprint","IMPRINT",FACE,{"disambiguationData":[TD([[makeQuery(id+"F18.imprint","IMPRINT",EDGE,{"derivedFrom":sQuery(id+"F18.wireOp",EDGE,"E138.0")}),1.0]])]});
            var Q11;
            Q11=makeQuery(id+"F16.opExtrude","SWEPT_FACE",FACE,{"disambiguationData":[OSD([sQuery(id+"F15.wireOp",EDGE,"E117")])]});
            extrude(context, id + "F19", {"entities" : qUnion([Q0, Q1, Q2, Q3, Q4, Q5, Q6, Q7, Q8, Q9, Q10]), "operationType" : NewBodyOperationType.REMOVE, "endBound" : BoundingType.UP_TO_SURFACE, "oppositeDirection" : true, "depth" : 25 * mm, "endBoundEntityFace" : qUnion([Q11]), "offsetDistance" : 25 * mm});
        }
        {
            var Q0;
            Q0=makeQuery(id+"F1.opExtrude","SWEPT_BODY",BODY,{"disambiguationData":[OSD([sQuery(id+"F0.wireOp",EDGE,"E0"),sQuery(id+"F0.wireOp",EDGE,"E1"),sQuery(id+"F0.wireOp",EDGE,"E2"),sQuery(id+"F0.wireOp",EDGE,"E3"),sQuery(id+"F0.wireOp",EDGE,"E5"),sQuery(id+"F0.wireOp",EDGE,"E6"),sQuery(id+"F0.wireOp",EDGE,"E7")])]});
            var Q1;
            Q1=qCreatedBy(id+"F12.planeOp",FACE);
            mirror(context, id + "F20", {"entities" : qUnion([Q0]), "mirrorPlane" : qUnion([Q1])});
        }
        {
            var Q0;
            Q0=makeQuery(id+"F1.opExtrude","CAP_FACE",FACE,{"disambiguationData":[OSD([sQuery(id+"F0.wireOp",EDGE,"E0"),sQuery(id+"F0.wireOp",EDGE,"E1"),sQuery(id+"F0.wireOp",EDGE,"E2"),sQuery(id+"F0.wireOp",EDGE,"E3"),sQuery(id+"F0.wireOp",EDGE,"E5"),sQuery(id+"F0.wireOp",EDGE,"E6"),sQuery(id+"F0.wireOp",EDGE,"E7")])],"isStart":false});
            var sketch = newSketch(context, id + "F21", { "sketchPlane" : qUnion([Q0])});
            skLineSegment(sketch, "E168", {"start": v(-411.35, 332.32) * mm, "end": v(-427.92, 292.32) * mm});
            skLineSegment(sketch, "E169", {"start": v(-427.92, 292.32) * mm, "end": v(-121.08, 292.32) * mm});
            skLineSegment(sketch, "E170", {"start": v(-121.08, 292.32) * mm, "end": v(-137.65, 332.32) * mm});
            skLineSegment(sketch, "E171", {"start": v(-137.65, 332.32) * mm, "end": v(-411.35, 332.32) * mm});
            skLineSegment(sketch, "E172", {"start": v(-507.02, 101.35) * mm, "end": v(-523.59, 61.35) * mm});
            skLineSegment(sketch, "E173", {"start": v(-523.59, 61.35) * mm, "end": v(-25.41, 61.35) * mm});
            skLineSegment(sketch, "E174", {"start": v(-25.41, 61.35) * mm, "end": v(-41.98, 101.35) * mm});
            skLineSegment(sketch, "E175", {"start": v(-41.98, 101.35) * mm, "end": v(-507.02, 101.35) * mm});
            skLineSegment(sketch, "E176", {"start": v(-419.63, 312.32) * mm, "end": v(-129.37, 312.32) * mm, "construction": true});
            skCircle(sketch, "E177", {"center": v(-388.4, 312.32) * mm, "radius": 6.25 * mm});
            skCircle(sketch, "E178", {"center": v(-274.5, 312.32) * mm, "radius": 6.25 * mm});
            skCircle(sketch, "E179", {"center": v(-160.6, 312.32) * mm, "radius": 6.25 * mm});
            skLineSegment(sketch, "E180", {"start": v(-515.3, 81.35) * mm, "end": v(-33.7, 81.35) * mm, "construction": true});
            skCircle(sketch, "E181", {"center": v(-484.08, 81.35) * mm, "radius": 6.25 * mm});
            skCircle(sketch, "E182", {"center": v(-274.5, 81.35) * mm, "radius": 6.25 * mm});
            skCircle(sketch, "E183", {"center": v(-64.92, 81.35) * mm, "radius": 6.25 * mm});
            skLineSegment(sketch, "E184", {"start": v(-358.92, 458.89) * mm, "end": v(-375.49, 418.89) * mm});
            skLineSegment(sketch, "E185", {"start": v(-375.49, 418.89) * mm, "end": v(-173.5, 418.89) * mm});
            skLineSegment(sketch, "E186", {"start": v(-173.5, 418.89) * mm, "end": v(-190.08, 458.89) * mm});
            skLineSegment(sketch, "E187", {"start": v(-190.08, 458.89) * mm, "end": v(-358.92, 458.89) * mm});
            skLineSegment(sketch, "E188", {"start": v(-367.2, 438.89) * mm, "end": v(-181.8, 438.89) * mm, "construction": true});
            skCircle(sketch, "E189", {"center": v(-213.02, 438.89) * mm, "radius": 6.25 * mm});
            skCircle(sketch, "E190", {"center": v(-335.98, 438.89) * mm, "radius": 6.25 * mm});
            skSolve(sketch);
        }
        {
            var Q0;
            Q0=qSketchRegion(id+"F21",true);
            extrude(context, id + "F22", {"entities" : qUnion([Q0]), "depth" : 4 * mm, "offsetDistance" : 25 * mm});
        }
        {
            var Q0;
            Q0=makeQuery(id+"F22.opExtrude","SWEPT_EDGE",EDGE,{"disambiguationData":[OSD([sQuery(id+"F21.wireOp",EDGE,"E172"),sQuery(id+"F21.wireOp",EDGE,"E173")])]});
            var Q1;
            Q1=makeQuery(id+"F22.opExtrude","SWEPT_EDGE",EDGE,{"disambiguationData":[OSD([sQuery(id+"F21.wireOp",EDGE,"E172"),sQuery(id+"F21.wireOp",EDGE,"E175")])]});
            var Q2;
            Q2=makeQuery(id+"F22.opExtrude","SWEPT_EDGE",EDGE,{"disambiguationData":[OSD([sQuery(id+"F21.wireOp",EDGE,"E173"),sQuery(id+"F21.wireOp",EDGE,"E174")])]});
            var Q3;
            Q3=makeQuery(id+"F22.opExtrude","SWEPT_EDGE",EDGE,{"disambiguationData":[OSD([sQuery(id+"F21.wireOp",EDGE,"E174"),sQuery(id+"F21.wireOp",EDGE,"E175")])]});
            var Q4;
            Q4=makeQuery(id+"F22.opExtrude","SWEPT_EDGE",EDGE,{"disambiguationData":[OSD([sQuery(id+"F21.wireOp",EDGE,"E170"),sQuery(id+"F21.wireOp",EDGE,"E171")])]});
            var Q5;
            Q5=makeQuery(id+"F22.opExtrude","SWEPT_EDGE",EDGE,{"disambiguationData":[OSD([sQuery(id+"F21.wireOp",EDGE,"E169"),sQuery(id+"F21.wireOp",EDGE,"E170")])]});
            var Q6;
            Q6=makeQuery(id+"F22.opExtrude","SWEPT_EDGE",EDGE,{"disambiguationData":[OSD([sQuery(id+"F21.wireOp",EDGE,"E168"),sQuery(id+"F21.wireOp",EDGE,"E169")])]});
            var Q7;
            Q7=makeQuery(id+"F22.opExtrude","SWEPT_EDGE",EDGE,{"disambiguationData":[OSD([sQuery(id+"F21.wireOp",EDGE,"E168"),sQuery(id+"F21.wireOp",EDGE,"E171")])]});
            var Q8;
            Q8=makeQuery(id+"F22.opExtrude","SWEPT_EDGE",EDGE,{"disambiguationData":[OSD([sQuery(id+"F21.wireOp",EDGE,"E184"),sQuery(id+"F21.wireOp",EDGE,"E187")])]});
            var Q9;
            Q9=makeQuery(id+"F22.opExtrude","SWEPT_EDGE",EDGE,{"disambiguationData":[OSD([sQuery(id+"F21.wireOp",EDGE,"E184"),sQuery(id+"F21.wireOp",EDGE,"E185")])]});
            var Q10;
            Q10=makeQuery(id+"F22.opExtrude","SWEPT_EDGE",EDGE,{"disambiguationData":[OSD([sQuery(id+"F21.wireOp",EDGE,"E186"),sQuery(id+"F21.wireOp",EDGE,"E187")])]});
            var Q11;
            Q11=makeQuery(id+"F22.opExtrude","SWEPT_EDGE",EDGE,{"disambiguationData":[OSD([sQuery(id+"F21.wireOp",EDGE,"E185"),sQuery(id+"F21.wireOp",EDGE,"E186")])]});
            fillet(context, id + "F23", {"entities" : qUnion([Q0, Q1, Q2, Q3, Q4, Q5, Q6, Q7, Q8, Q9, Q10, Q11]), "radius" : 10 * mm, "tangentPropagation" : true, "allowEdgeOverflow" : false});
        }
        {
            var Q0;
            Q0=makeQuery(id+"F22.opExtrude","SWEPT_BODY",BODY,{"disambiguationData":[OSD([sQuery(id+"F21.wireOp",EDGE,"E172"),sQuery(id+"F21.wireOp",EDGE,"E173"),sQuery(id+"F21.wireOp",EDGE,"E174"),sQuery(id+"F21.wireOp",EDGE,"E175"),sQuery(id+"F21.wireOp",EDGE,"E181"),sQuery(id+"F21.wireOp",EDGE,"E182"),sQuery(id+"F21.wireOp",EDGE,"E183")])]});
            var Q1;
            Q1=makeQuery(id+"F22.opExtrude","SWEPT_BODY",BODY,{"disambiguationData":[OSD([sQuery(id+"F21.wireOp",EDGE,"E168"),sQuery(id+"F21.wireOp",EDGE,"E169"),sQuery(id+"F21.wireOp",EDGE,"E170"),sQuery(id+"F21.wireOp",EDGE,"E171"),sQuery(id+"F21.wireOp",EDGE,"E177"),sQuery(id+"F21.wireOp",EDGE,"E178"),sQuery(id+"F21.wireOp",EDGE,"E179")])]});
            var Q2;
            Q2=makeQuery(id+"F22.opExtrude","SWEPT_BODY",BODY,{"disambiguationData":[OSD([sQuery(id+"F21.wireOp",EDGE,"E184"),sQuery(id+"F21.wireOp",EDGE,"E185"),sQuery(id+"F21.wireOp",EDGE,"E186"),sQuery(id+"F21.wireOp",EDGE,"E187"),sQuery(id+"F21.wireOp",EDGE,"E189"),sQuery(id+"F21.wireOp",EDGE,"E190")])]});
            var Q3;
            Q3=qCreatedBy(id+"F13.planeOp",FACE);
            mirror(context, id + "F24", {"entities" : qUnion([Q0, Q1, Q2]), "mirrorPlane" : qUnion([Q3])});
        }
        {
            var Q0;
            Q0=makeQuery(id+"F8.opExtrude","CAP_FACE",FACE,{"disambiguationData":[OSD([sQuery(id+"F7.wireOp",EDGE,"E57"),sQuery(id+"F7.wireOp",EDGE,"E58"),sQuery(id+"F7.wireOp",EDGE,"E59"),sQuery(id+"F7.wireOp",EDGE,"E60"),sQuery(id+"F7.wireOp",EDGE,"E63"),sQuery(id+"F7.wireOp",EDGE,"E65"),sQuery(id+"F7.wireOp",EDGE,"E66"),sQuery(id+"F7.wireOp",EDGE,"E67"),sQuery(id+"F7.wireOp",EDGE,"E68"),sQuery(id+"F7.wireOp",EDGE,"E69")])],"isStart":true});
            cPlane(context, id + "F25", {"entities" : qUnion([Q0]), "cplaneType" : CPlaneType.OFFSET, "offset" : 300 * mm, "width" : 150 * mm, "height" : 150 * mm});
        }
        {
            var Q0;
            Q0=qCreatedBy(id+"F13.planeOp",FACE);
            var sketch = newSketch(context, id + "F26", { "sketchPlane" : qUnion([Q0])});
            skCircle(sketch, "E191", {"center": v(274.5, 920) * mm, "radius": 6.25 * mm});
            skCircle(sketch, "E192", {"center": v(274.5, 920) * mm, "radius": 10 * mm});
            skSolve(sketch);
        }
        {
            var Q0;
            Q0 = qSketchRegion(id + "F26", true);
            extrude(context, id + "F27", {"entities" : qUnion([Q0]), "depth" : 62 * mm, "offsetDistance" : 25 * mm, "symmetric" : true});
        }
        {
            var Q0;
            Q0=makeQuery(id+"F1.opExtrude","SWEPT_BODY",BODY,{"disambiguationData":[OSD([sQuery(id+"F0.wireOp",EDGE,"E0"),sQuery(id+"F0.wireOp",EDGE,"E1"),sQuery(id+"F0.wireOp",EDGE,"E2"),sQuery(id+"F0.wireOp",EDGE,"E3"),sQuery(id+"F0.wireOp",EDGE,"E5"),sQuery(id+"F0.wireOp",EDGE,"E6"),sQuery(id+"F0.wireOp",EDGE,"E7")])]});
            var Q1;
            Q1=makeQuery(id+"F20.opPattern","COPY",BODY,{"derivedFrom":makeQuery(id+"F1.opExtrude","SWEPT_BODY",BODY,{"disambiguationData":[OSD([sQuery(id+"F0.wireOp",EDGE,"E0"),sQuery(id+"F0.wireOp",EDGE,"E1"),sQuery(id+"F0.wireOp",EDGE,"E2"),sQuery(id+"F0.wireOp",EDGE,"E3"),sQuery(id+"F0.wireOp",EDGE,"E5"),sQuery(id+"F0.wireOp",EDGE,"E6"),sQuery(id+"F0.wireOp",EDGE,"E7")])]}),"instanceName":"1"});
            var Q2;
            Q2=makeQuery(id+"F22.opExtrude","SWEPT_BODY",BODY,{"disambiguationData":[OSD([sQuery(id+"F21.wireOp",EDGE,"E172"),sQuery(id+"F21.wireOp",EDGE,"E173"),sQuery(id+"F21.wireOp",EDGE,"E174"),sQuery(id+"F21.wireOp",EDGE,"E175"),sQuery(id+"F21.wireOp",EDGE,"E181"),sQuery(id+"F21.wireOp",EDGE,"E182"),sQuery(id+"F21.wireOp",EDGE,"E183")])]});
            var Q3;
            Q3=makeQuery(id+"F22.opExtrude","SWEPT_BODY",BODY,{"disambiguationData":[OSD([sQuery(id+"F21.wireOp",EDGE,"E168"),sQuery(id+"F21.wireOp",EDGE,"E169"),sQuery(id+"F21.wireOp",EDGE,"E170"),sQuery(id+"F21.wireOp",EDGE,"E171"),sQuery(id+"F21.wireOp",EDGE,"E177"),sQuery(id+"F21.wireOp",EDGE,"E178"),sQuery(id+"F21.wireOp",EDGE,"E179")])]});
            var Q4;
            Q4=makeQuery(id+"F22.opExtrude","SWEPT_BODY",BODY,{"disambiguationData":[OSD([sQuery(id+"F21.wireOp",EDGE,"E184"),sQuery(id+"F21.wireOp",EDGE,"E185"),sQuery(id+"F21.wireOp",EDGE,"E186"),sQuery(id+"F21.wireOp",EDGE,"E187"),sQuery(id+"F21.wireOp",EDGE,"E189"),sQuery(id+"F21.wireOp",EDGE,"E190")])]});
            var Q5;
            Q5=makeQuery(id+"F24.opPattern","COPY",BODY,{"derivedFrom":makeQuery(id+"F22.opExtrude","SWEPT_BODY",BODY,{"disambiguationData":[OSD([sQuery(id+"F21.wireOp",EDGE,"E168"),sQuery(id+"F21.wireOp",EDGE,"E169"),sQuery(id+"F21.wireOp",EDGE,"E170"),sQuery(id+"F21.wireOp",EDGE,"E171"),sQuery(id+"F21.wireOp",EDGE,"E177"),sQuery(id+"F21.wireOp",EDGE,"E178"),sQuery(id+"F21.wireOp",EDGE,"E179")])]}),"instanceName":"1"});
            var Q6;
            Q6=makeQuery(id+"F24.opPattern","COPY",BODY,{"derivedFrom":makeQuery(id+"F22.opExtrude","SWEPT_BODY",BODY,{"disambiguationData":[OSD([sQuery(id+"F21.wireOp",EDGE,"E184"),sQuery(id+"F21.wireOp",EDGE,"E185"),sQuery(id+"F21.wireOp",EDGE,"E186"),sQuery(id+"F21.wireOp",EDGE,"E187"),sQuery(id+"F21.wireOp",EDGE,"E189"),sQuery(id+"F21.wireOp",EDGE,"E190")])]}),"instanceName":"1"});
            var Q7;
            Q7=makeQuery(id+"F24.opPattern","COPY",BODY,{"derivedFrom":makeQuery(id+"F22.opExtrude","SWEPT_BODY",BODY,{"disambiguationData":[OSD([sQuery(id+"F21.wireOp",EDGE,"E172"),sQuery(id+"F21.wireOp",EDGE,"E173"),sQuery(id+"F21.wireOp",EDGE,"E174"),sQuery(id+"F21.wireOp",EDGE,"E175"),sQuery(id+"F21.wireOp",EDGE,"E181"),sQuery(id+"F21.wireOp",EDGE,"E182"),sQuery(id+"F21.wireOp",EDGE,"E183")])]}),"instanceName":"1"});
            var Q8;
            Q8=makeQuery(id+"F8.opExtrude","SWEPT_BODY",BODY,{"disambiguationData":[OSD([sQuery(id+"F7.wireOp",EDGE,"E57"),sQuery(id+"F7.wireOp",EDGE,"E58"),sQuery(id+"F7.wireOp",EDGE,"E59"),sQuery(id+"F7.wireOp",EDGE,"E60"),sQuery(id+"F7.wireOp",EDGE,"E63"),sQuery(id+"F7.wireOp",EDGE,"E65"),sQuery(id+"F7.wireOp",EDGE,"E66"),sQuery(id+"F7.wireOp",EDGE,"E67"),sQuery(id+"F7.wireOp",EDGE,"E68"),sQuery(id+"F7.wireOp",EDGE,"E69")])]});
            var Q9;
            Q9=makeQuery(id+"F16.opExtrude","SWEPT_BODY",BODY,{"disambiguationData":[OSD([sQuery(id+"F15.wireOp",EDGE,"E116"),sQuery(id+"F15.wireOp",EDGE,"E117"),sQuery(id+"F15.wireOp",EDGE,"E118"),sQuery(id+"F15.wireOp",EDGE,"E119"),sQuery(id+"F15.wireOp",EDGE,"E121"),sQuery(id+"F15.wireOp",EDGE,"E122"),sQuery(id+"F15.wireOp",EDGE,"E123"),sQuery(id+"F15.wireOp",EDGE,"E124"),sQuery(id+"F15.wireOp",EDGE,"E125"),sQuery(id+"F15.wireOp",EDGE,"E126"),sQuery(id+"F15.wireOp",EDGE,"E127"),sQuery(id+"F15.wireOp",EDGE,"E128"),sQuery(id+"F15.wireOp",EDGE,"E129")])]});
            var Q10;
            Q10=makeQuery(id+"F27.opExtrude","SWEPT_BODY",BODY,{"disambiguationData":[OSD([sQuery(id+"F26.wireOp",EDGE,"E191"),sQuery(id+"F26.wireOp",EDGE,"E192")])]});
            var Q11;
            Q11=qCreatedBy(id+"F25.planeOp",FACE);
            mirror(context, id + "F28", {"entities" : qUnion([Q0, Q1, Q2, Q3, Q4, Q5, Q6, Q7, Q8, Q9, Q10]), "mirrorPlane" : qUnion([Q11])});
        }
        {
            var Q0;
            {var subQ0=sQuery(id+"F0.wireOp",EDGE,"E3");Q0=makeQuery(id+"F6.boolean.opBoolean","SPLIT",FACE,{"disambiguationData":[TD([makeQuery(id+"F6.opExtrude","SWEPT_FACE",FACE,{"disambiguationData":[OSD([sQuery(id+"F5.wireOp",EDGE,"E46.MirrorCS")])]})])],"derivedFrom":makeQuery(id+"F1.opExtrude","SWEPT_FACE",FACE,{"disambiguationData":[OSD([subQ0])]})});}
            var sketch = newSketch(context, id + "F29", { "sketchPlane" : qUnion([Q0])});
            skLineSegment(sketch, "E193", {"start": v(-720, 130) * mm, "end": v(0, 130) * mm});
            skLineSegment(sketch, "E194", {"start": v(0, 130) * mm, "end": v(0, 170) * mm});
            skLineSegment(sketch, "E195", {"start": v(0, 170) * mm, "end": v(-720, 170) * mm});
            skLineSegment(sketch, "E196", {"start": v(-720, 170) * mm, "end": v(-720, 130) * mm});
            skLineSegment(sketch, "E197", {"start": v(-720, 150) * mm, "end": v(0, 150) * mm, "construction": true});
            skCircle(sketch, "E198", {"center": v(-690, 150) * mm, "radius": 6.25 * mm});
            skCircle(sketch, "E199", {"center": v(-30, 150) * mm, "radius": 6.25 * mm});
            skLineSegment(sketch, "E200", {"start": v(0, 320) * mm, "end": v(-720, 320) * mm});
            skLineSegment(sketch, "E201", {"start": v(-720, 320) * mm, "end": v(-720, 280) * mm});
            skLineSegment(sketch, "E202", {"start": v(-720, 280) * mm, "end": v(0, 280) * mm});
            skLineSegment(sketch, "E203", {"start": v(0, 280) * mm, "end": v(0, 320) * mm});
            skLineSegment(sketch, "E204", {"start": v(0, 300) * mm, "end": v(-720, 300) * mm, "construction": true});
            skCircle(sketch, "E205", {"center": v(-690, 300) * mm, "radius": 6.25 * mm});
            skCircle(sketch, "E206", {"center": v(-30, 300) * mm, "radius": 6.25 * mm});
            skSolve(sketch);
        }
        {
            var Q0;
            Q0=qSketchRegion(id+"F29",true);
            extrude(context, id + "F30", {"entities" : qUnion([Q0]), "depth" : 4 * mm, "offsetDistance" : 25 * mm});
        }
        {
            var Q0;
            Q0=makeQuery(id+"F30.opExtrude","SWEPT_EDGE",EDGE,{"disambiguationData":[OSD([sQuery(id+"F29.wireOp",EDGE,"E195"),sQuery(id+"F29.wireOp",EDGE,"E196")])]});
            var Q1;
            Q1=makeQuery(id+"F30.opExtrude","SWEPT_EDGE",EDGE,{"disambiguationData":[OSD([sQuery(id+"F29.wireOp",EDGE,"E193"),sQuery(id+"F29.wireOp",EDGE,"E196")])]});
            var Q2;
            Q2=makeQuery(id+"F30.opExtrude","SWEPT_EDGE",EDGE,{"disambiguationData":[OSD([sQuery(id+"F29.wireOp",EDGE,"E194"),sQuery(id+"F29.wireOp",EDGE,"E195")])]});
            var Q3;
            Q3=makeQuery(id+"F30.opExtrude","SWEPT_EDGE",EDGE,{"disambiguationData":[OSD([sQuery(id+"F29.wireOp",EDGE,"E193"),sQuery(id+"F29.wireOp",EDGE,"E194")])]});
            var Q4;
            Q4=makeQuery(id+"F30.opExtrude","SWEPT_EDGE",EDGE,{"disambiguationData":[OSD([sQuery(id+"F29.wireOp",EDGE,"E200"),sQuery(id+"F29.wireOp",EDGE,"E201")])]});
            var Q5;
            Q5=makeQuery(id+"F30.opExtrude","SWEPT_EDGE",EDGE,{"disambiguationData":[OSD([sQuery(id+"F29.wireOp",EDGE,"E201"),sQuery(id+"F29.wireOp",EDGE,"E202")])]});
            var Q6;
            Q6=makeQuery(id+"F30.opExtrude","SWEPT_EDGE",EDGE,{"disambiguationData":[OSD([sQuery(id+"F29.wireOp",EDGE,"E202"),sQuery(id+"F29.wireOp",EDGE,"E203")])]});
            var Q7;
            Q7=makeQuery(id+"F30.opExtrude","SWEPT_EDGE",EDGE,{"disambiguationData":[OSD([sQuery(id+"F29.wireOp",EDGE,"E200"),sQuery(id+"F29.wireOp",EDGE,"E203")])]});
            fillet(context, id + "F31", {"entities" : qUnion([Q0, Q1, Q2, Q3, Q4, Q5, Q6, Q7]), "radius" : 10 * mm, "tangentPropagation" : true, "allowEdgeOverflow" : false});
        }
        {
            var Q0;
            Q0=makeQuery(id+"F19.boolean.opBoolean","COPY",FACE,{"derivedFrom":makeQuery(id+"F19.opExtrude","SWEPT_FACE",FACE,{"disambiguationData":[OSD([sQuery(id+"F18.wireOp",EDGE,"E140"),sQuery(id+"F18.wireOp",EDGE,"E158.MirrorCS")])]})});
            var Q1;
            Q1=makeQuery(id+"F19.boolean.opBoolean","COPY",FACE,{"derivedFrom":makeQuery(id+"F19.opExtrude","SWEPT_FACE",FACE,{"disambiguationData":[OSD([sQuery(id+"F18.wireOp",EDGE,"E147.MirrorCS"),sQuery(id+"F18.wireOp",EDGE,"E166.MirrorCS")])]})});
            cPlane(context, id + "F32", {"entities" : qUnion([Q0, Q1]), "cplaneType" : CPlaneType.MID_PLANE, "offset" : 25 * mm, "width" : 150 * mm, "height" : 150 * mm});
        }
        {
            var Q0;
            Q0=makeQuery(id+"F30.opExtrude","SWEPT_BODY",BODY,{"disambiguationData":[OSD([sQuery(id+"F29.wireOp",EDGE,"E193"),sQuery(id+"F29.wireOp",EDGE,"E194"),sQuery(id+"F29.wireOp",EDGE,"E195"),sQuery(id+"F29.wireOp",EDGE,"E196"),sQuery(id+"F29.wireOp",EDGE,"E198"),sQuery(id+"F29.wireOp",EDGE,"E199")])]});
            var Q1;
            Q1=makeQuery(id+"F30.opExtrude","SWEPT_BODY",BODY,{"disambiguationData":[OSD([sQuery(id+"F29.wireOp",EDGE,"E200"),sQuery(id+"F29.wireOp",EDGE,"E201"),sQuery(id+"F29.wireOp",EDGE,"E202"),sQuery(id+"F29.wireOp",EDGE,"E203"),sQuery(id+"F29.wireOp",EDGE,"E205"),sQuery(id+"F29.wireOp",EDGE,"E206")])]});
            var Q2;
            Q2=qCreatedBy(id+"F32.planeOp",FACE);
            mirror(context, id + "F33", {"entities" : qUnion([Q0, Q1]), "mirrorPlane" : qUnion([Q2])});
        }
        {
            var Q0;
            Q0=qCreatedBy(id+"F25.planeOp",FACE);
            var sketch = newSketch(context, id + "F34", { "sketchPlane" : qUnion([Q0])});
            skCircle(sketch, "E207", {"center": v(-274.5, 920) * mm, "radius": 5.9 * mm});
            skSolve(sketch);
        }
        {
            var Q0;
            Q0=qSketchRegion(id+"F34",true);
            extrude(context, id + "F35", {"entities" : qUnion([Q0]), "depth" : 765 * mm, "offsetDistance" : 25 * mm, "symmetric" : true});
        }
        {
            var Q0;
            Q0=qCreatedBy(id+"F25.planeOp",FACE);
            var sketch = newSketch(context, id + "F36", { "sketchPlane" : qUnion([Q0])});
            skCircle(sketch, "E208", {"center": v(-274.5, 920) * mm, "radius": 30 * mm});
            skCircle(sketch, "E209", {"center": v(-274.5, 920) * mm, "radius": 6.25 * mm});
            skSolve(sketch);
        }
        {
            var Q0;
            Q0 = qSketchRegion(id + "F36", true);
            extrude(context, id + "F37", {"entities" : qUnion([Q0]), "depth" : 590 * mm, "offsetDistance" : 25 * mm, "symmetric" : true});
        }
        {
            var Q0;
            Q0=makeQuery(id+"F35.opExtrude","CAP_EDGE",EDGE,{"disambiguationData":[OSD([sQuery(id+"F34.wireOp",EDGE,"E207")])],"isStart":false});
            var Q1;
            Q1=makeQuery(id+"F35.opExtrude","CAP_EDGE",EDGE,{"disambiguationData":[OSD([sQuery(id+"F34.wireOp",EDGE,"E207")])],"isStart":true});
            chamfer(context, id + "F38", {"entities" : qUnion([Q0, Q1]), "width" : 2 * mm, "tangentPropagation" : true});
        }
        {
            var Q0;
            Q0=makeQuery(id+"F37.opExtrude","SWEPT_FACE",FACE,{"disambiguationData":[OSD([sQuery(id+"F36.wireOp",EDGE,"E208")])]});
            cPlane(context, id + "F39", {"entities" : qUnion([Q0]), "cplaneType" : CPlaneType.LINE_ANGLE, "offset" : 25 * mm, "angle" : 0 * degree, "width" : 150 * mm, "height" : 150 * mm});
        }
        {
            var Q0;
            Q0=makeQuery(id+"F37.opExtrude","CAP_EDGE",EDGE,{"disambiguationData":[OSD([sQuery(id+"F36.wireOp",EDGE,"E208")])],"isStart":false});
            var Q1;
            Q1=makeQuery(id+"F37.opExtrude","CAP_EDGE",EDGE,{"disambiguationData":[OSD([sQuery(id+"F36.wireOp",EDGE,"E208")])],"isStart":true});
            chamfer(context, id + "F40", {"entities" : qUnion([Q0, Q1]), "width" : 5 * mm, "tangentPropagation" : true});
        }
    });
